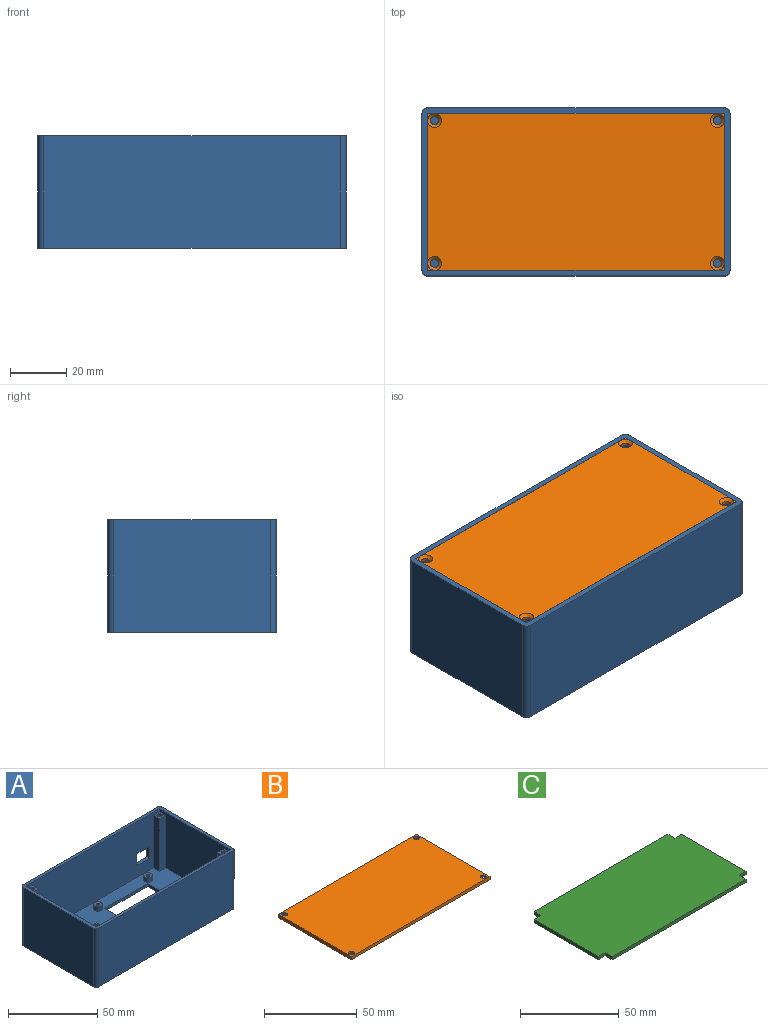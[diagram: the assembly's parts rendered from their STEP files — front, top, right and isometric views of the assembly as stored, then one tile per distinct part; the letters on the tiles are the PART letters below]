
ASSEMBLY  parts=3 mates=3
PART A: 61 faces, bbox 110x60x40 mm
  f0: plane 106x40mm, normal (0,1,0), area 4160mm2, adj f5,f6,f53,f54,f55,f56,f58,f59
  f1: plane 106x38mm, normal (0,-1,0), area 3588mm2, adj f2,f3,f6,f10,f32,f34,f46,f49
  f2: plane 56x38mm, normal (1,0,0), area 1768mm2, adj f1,f3,f4,f6,f41,f44,f47,f49
  f3: plane 106x56mm, normal (0,0,1), area 4278mm2, adj f1,f2,f4,f10,f11,f12,f13,f14
  f4: plane 106x38mm, normal (0,1,0), area 3668mm2, adj f2,f3,f6,f10,f37,f39,f42,f44
  f5: plane 110x60mm, normal (0,0,-1), area 5117.1mm2, adj f0,f7,f8,f9,f11,f12,f13,f14
  f6: plane 110x60mm, normal (0,0,1), area 660.6mm2, adj f0,f1,f2,f4,f7,f8,f9,f10
  f7: plane 106x40mm, normal (0,-1,0), area 4240mm2, adj f5,f6,f57,f60
  f8: plane 56x40mm, normal (1,0,0), area 2240mm2, adj f5,f6,f57,f58
  f9: plane 56x40mm, normal (-1,0,0), area 2240mm2, adj f5,f6,f59,f60
  f10: plane 56x38mm, normal (-1,0,0), area 1768mm2, adj f1,f3,f4,f6,f31,f34,f36,f39
  f11: plane 34x2mm, normal (0,1,0), area 68mm2, adj f3,f5,f12,f14
  f12: plane 39x2mm, normal (1,0,0), area 78mm2, adj f3,f5,f11,f13
  f13: plane 34x2mm, normal (0,-1,0), area 68mm2, adj f3,f5,f12,f14
  f14: plane 39x2mm, normal (-1,0,0), area 78mm2, adj f3,f5,f11,f13
  f15: cylinder r=1mm len=3mm, axis (0,0,-1), area 18.8mm2, adj f17,f18
  f16: cylinder r=2.5mm len=5mm, axis (0,0,-1), area 47.1mm2, adj f3,f17
  f17: plane 5x5mm, normal (0,0,1), area 16.5mm2, adj f15,f16
  f18: plane 2x2mm, normal (0,0,1), area 3.1mm2, adj f15
  f19: cylinder r=2.5mm len=5mm, axis (0,0,-1), area 47.1mm2, adj f3,f21
  f20: cylinder r=1mm len=3mm, axis (0,0,-1), area 18.8mm2, adj f21,f22
  f21: plane 5x5mm, normal (0,0,1), area 16.5mm2, adj f19,f20
  f22: plane 2x2mm, normal (0,0,1), area 3.1mm2, adj f20
  f23: cylinder r=2.5mm len=5mm, axis (0,0,-1), area 47.1mm2, adj f3,f25
  f24: cylinder r=1mm len=3mm, axis (0,0,-1), area 18.8mm2, adj f25,f26
  f25: plane 5x5mm, normal (0,0,1), area 16.5mm2, adj f23,f24
  f26: plane 2x2mm, normal (0,0,1), area 3.1mm2, adj f24
  f27: cylinder r=1mm len=3mm, axis (0,0,-1), area 18.8mm2, adj f29,f30
  f28: cylinder r=2.5mm len=5mm, axis (0,0,-1), area 47.1mm2, adj f3,f29
  f29: plane 5x5mm, normal (0,0,1), area 16.5mm2, adj f27,f28
  f30: plane 2x2mm, normal (0,0,1), area 3.1mm2, adj f27
  f31: plane 36x5mm, normal (0,-1,0), area 180mm2, adj f3,f10,f32,f34
  f32: plane 36x5mm, normal (-1,0,0), area 180mm2, adj f1,f3,f31,f34
  f33: cylinder r=1.5mm len=36mm, axis (0,0,-1), area 339.3mm2, adj f34,f35
  f34: plane 5x5mm, normal (0,0,1), area 17.9mm2, adj f1,f10,f31,f32,f33
  f35: plane 3x3mm, normal (0,0,1), area 7.1mm2, adj f33
  f36: plane 36x5mm, normal (0,1,0), area 180mm2, adj f3,f10,f37,f39
  f37: plane 36x5mm, normal (-1,0,0), area 180mm2, adj f3,f4,f36,f39
  f38: cylinder r=1.5mm len=36mm, axis (0,0,-1), area 339.3mm2, adj f39,f40
  f39: plane 5x5mm, normal (0,0,1), area 17.9mm2, adj f4,f10,f36,f37,f38
  f40: plane 3x3mm, normal (0,0,1), area 7.1mm2, adj f38
  f41: plane 36x5mm, normal (0,1,0), area 180mm2, adj f2,f3,f42,f44
  f42: plane 36x5mm, normal (1,0,0), area 180mm2, adj f3,f4,f41,f44
  f43: cylinder r=1.5mm len=36mm, axis (0,0,-1), area 339.3mm2, adj f44,f45
  f44: plane 5x5mm, normal (0,0,1), area 17.9mm2, adj f2,f4,f41,f42,f43
  f45: plane 3x3mm, normal (0,0,1), area 7.1mm2, adj f43
  f46: plane 36x5mm, normal (1,0,0), area 180mm2, adj f1,f3,f47,f49
  f47: plane 36x5mm, normal (0,-1,0), area 180mm2, adj f2,f3,f46,f49
  f48: cylinder r=1.5mm len=36mm, axis (0,0,-1), area 339.3mm2, adj f49,f50
  f49: plane 5x5mm, normal (0,0,1), area 17.9mm2, adj f1,f2,f46,f47,f48
  f50: plane 3x3mm, normal (0,0,1), area 7.1mm2, adj f48
  f51: cylinder r=4.94mm len=9.89mm, axis (0,0,-1), area 62.1mm2, adj f3,f5
  f52: cylinder r=4.94mm len=9.89mm, axis (0,0,-1), area 62.1mm2, adj f3,f5
  f53: plane 8x2mm, normal (-1,0,0), area 16mm2, adj f0,f1,f54,f56
  f54: plane 10x2mm, normal (0,0,1), area 20mm2, adj f0,f1,f53,f55
  f55: plane 8x2mm, normal (1,0,0), area 16mm2, adj f0,f1,f54,f56
  f56: plane 10x2mm, normal (0,0,-1), area 20mm2, adj f0,f1,f53,f55
  f57: cylinder r=2mm len=40mm, axis (0,0,1), area 125.7mm2, adj f5,f6,f7,f8
  f58: cylinder r=2mm len=40mm, axis (0,0,-1), area 125.7mm2, adj f0,f5,f6,f8
  f59: cylinder r=2mm len=40mm, axis (0,0,1), area 125.7mm2, adj f0,f5,f6,f9
  f60: cylinder r=2mm len=40mm, axis (0,0,-1), area 125.7mm2, adj f5,f6,f7,f9
PART B: 18 faces, bbox 106x56x2 mm
  f0: plane 2.5x2.5mm, normal (0,0,-1), area 1.3mm2, adj f6,f11,f14
  f1: plane 2.5x2.5mm, normal (0,0,-1), area 1.3mm2, adj f4,f11,f15
  f2: plane 106x56mm, normal (0,0,-1), area 5852.1mm2, adj f4,f5,f6,f11,f14,f15,f16,f17
  f3: plane 2.5x2.5mm, normal (0,0,-1), area 1.3mm2, adj f5,f6,f17
  f4: plane 106x2mm, normal (0,-1,0), area 212mm2, adj f1,f2,f5,f11,f12,f13
  f5: plane 56x2mm, normal (1,0,0), area 112mm2, adj f2,f3,f4,f6,f12,f13
  f6: plane 106x2mm, normal (0,1,0), area 212mm2, adj f0,f2,f3,f5,f11,f12
  f7: cylinder r=1.5mm len=3mm, axis (0,0,-1), area 9.4mm2, adj f12,f14
  f8: cylinder r=1.5mm len=3mm, axis (0,0,-1), area 9.4mm2, adj f12,f17
  f9: cylinder r=1.5mm len=3mm, axis (0,0,-1), area 9.4mm2, adj f12,f16
  f10: cylinder r=1.5mm len=3mm, axis (0,0,-1), area 9.4mm2, adj f12,f15
  f11: plane 56x2mm, normal (-1,0,0), area 112mm2, adj f0,f1,f2,f4,f6,f12
  f12: plane 106x56mm, normal (0,0,1), area 5907.7mm2, adj f4,f5,f6,f7,f8,f9,f10,f11
  f13: plane 2.5x2.5mm, normal (0,0,-1), area 1.3mm2, adj f4,f5,f16
  f14: cone r=2.5mm half-angle=45deg, axis (0,0,-1), area 17.8mm2, adj f0,f2,f7
  f15: cone r=1.5mm half-angle=45deg, axis (0,0,-1), area 17.8mm2, adj f1,f2,f10
  f16: cone r=2.5mm half-angle=45deg, axis (0,0,-1), area 17.8mm2, adj f2,f9,f13
  f17: cone r=1.5mm half-angle=45deg, axis (0,0,-1), area 17.8mm2, adj f2,f3,f8
PART C: 14 faces, bbox 106x56x2 mm
  f0: plane 5x2mm, normal (1,0,0), area 10mm2, adj f1,f11,f12,f13
  f1: plane 96x2mm, normal (0,1,0), area 192mm2, adj f0,f2,f12,f13
  f2: plane 5x2mm, normal (-1,0,0), area 10mm2, adj f1,f3,f12,f13
  f3: plane 5x2mm, normal (0,1,0), area 10mm2, adj f2,f4,f12,f13
  f4: plane 46x2mm, normal (-1,0,0), area 92mm2, adj f3,f5,f12,f13
  f5: plane 5x2mm, normal (0,-1,0), area 10mm2, adj f4,f6,f12,f13
  f6: plane 5x2mm, normal (-1,0,0), area 10mm2, adj f5,f7,f12,f13
  f7: plane 96x2mm, normal (0,-1,0), area 192mm2, adj f6,f8,f12,f13
  f8: plane 5x2mm, normal (1,0,0), area 10mm2, adj f7,f9,f12,f13
  f9: plane 5x2mm, normal (0,-1,0), area 10mm2, adj f8,f10,f12,f13
  f10: plane 46x2mm, normal (1,0,0), area 92mm2, adj f9,f11,f12,f13
  f11: plane 5x2mm, normal (0,1,0), area 10mm2, adj f0,f10,f12,f13
  f12: plane 106x56mm, normal (0,0,1), area 5836mm2, adj f0,f1,f2,f3,f4,f5,f6,f7
  f13: plane 106x56mm, normal (0,0,-1), area 5836mm2, adj f0,f1,f2,f3,f4,f5,f6,f7
PLACE A t=(-43.52,-29.24,11.28)mm fixed
PLACE B rot(axis=(0,1,0),180deg) t=(-43.52,-29.24,51.28)mm
PLACE C t=(-43.52,-29.24,35.65)mm
MATE planar C.f7 <-> A.f4  axis (0,-1,0) through (-43.52,-57.24,36.65)mm
MATE fastened B.f9 <-> A.f43  axis (0,0,-1) through (-94.02,-54.74,49.28)mm
MATE planar C.f10 <-> A.f10  axis (1,0,0) through (9.48,-29.24,36.65)mm
